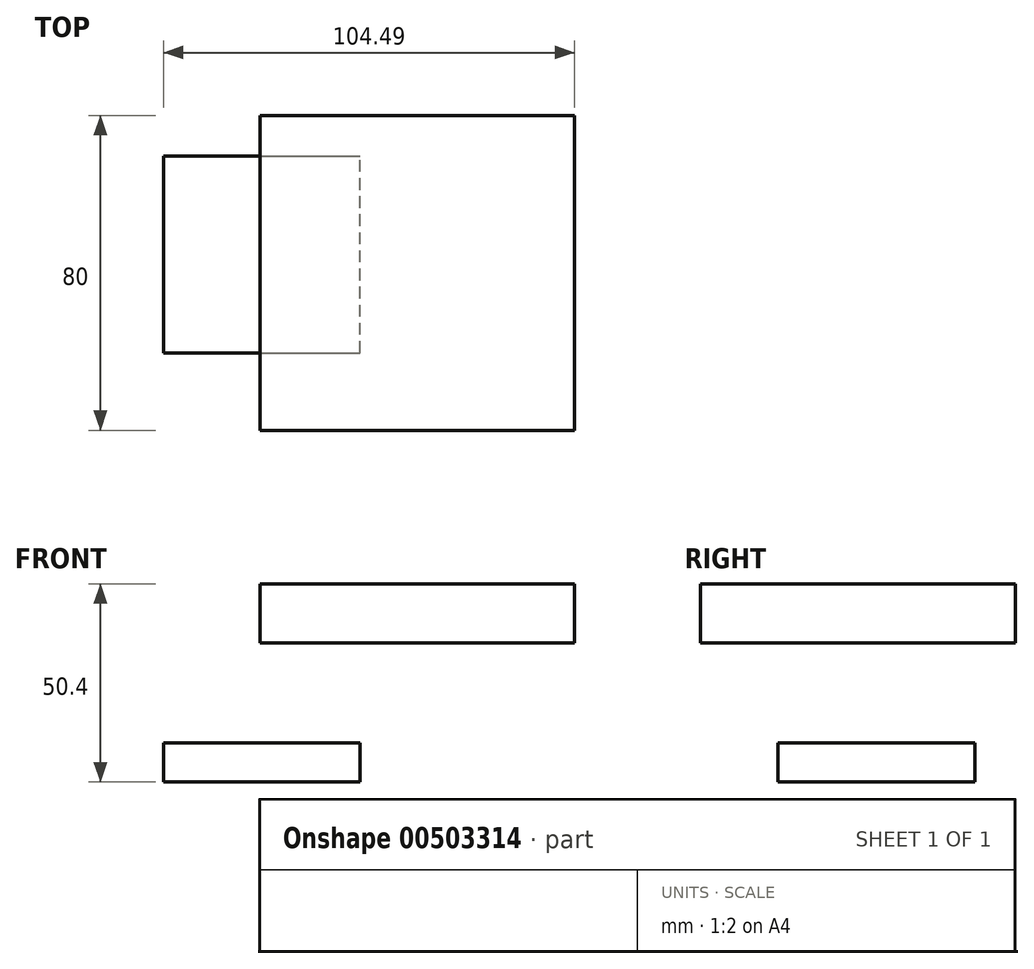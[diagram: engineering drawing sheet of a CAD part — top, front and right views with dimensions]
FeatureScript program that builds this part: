
annotation { "Feature Type Name" : "Feature", "Feature Type Description" : "" }
export const myFeature = defineFeature(function(context is Context, id is Id, definition is map)
    precondition{}
    {
        {
            var Q0;
            Q0=qCreatedBy(makeId("Top.planeOp"),FACE);
            var sketch = newSketch(context, id + "F0", { "sketchPlane" : qUnion([Q0])});
            skLineSegment(sketch, "E0.bottom", {"start": v(0, 0) * mm, "end": v(80, 0) * mm});
            skLineSegment(sketch, "E0.top", {"start": v(0, -80) * mm, "end": v(80, -80) * mm});
            skLineSegment(sketch, "E0.left", {"start": v(0, 0) * mm, "end": v(0, -80) * mm});
            skLineSegment(sketch, "E0.right", {"start": v(80, 0) * mm, "end": v(80, -80) * mm});
            skSolve(sketch);
        }
        {
            var Q0;
            Q0=makeQuery(id+"F0.imprint","IMPRINT",FACE,{"disambiguationData":[TD([[makeQuery(id+"F0.imprint","IMPRINT",EDGE,{"derivedFrom":sQuery(id+"F0.wireOp",EDGE,"E0.bottom")}),-1.0]])]});
            extrude(context, id + "F1", {"entities" : qUnion([Q0]), "depth" : 15 * mm, "offsetDistance" : 25.4 * mm});
        }
        {
            var Q0;
            Q0=makeQuery(id+"F1.opExtrude","CAP_FACE",FACE,{"disambiguationData":[OSD([sQuery(id+"F0.wireOp",EDGE,"E0.bottom"),sQuery(id+"F0.wireOp",EDGE,"E0.top"),sQuery(id+"F0.wireOp",EDGE,"E0.left"),sQuery(id+"F0.wireOp",EDGE,"E0.right")])],"isStart":true});
            cPlane(context, id + "F2", {"entities" : qUnion([Q0]), "cplaneType" : CPlaneType.OFFSET, "offset" : 25.4 * mm, "width" : 152.4 * mm, "height" : 152.4 * mm});
        }
        {
            var Q0;
            Q0=qCreatedBy(id+"F2.planeOp",FACE);
            var sketch = newSketch(context, id + "F3", { "sketchPlane" : qUnion([Q0])});
            skLineSegment(sketch, "E1.bottom", {"start": v(-24.5, 60.32) * mm, "end": v(25.5, 60.32) * mm});
            skLineSegment(sketch, "E1.top", {"start": v(-24.5, 10.32) * mm, "end": v(25.5, 10.32) * mm});
            skLineSegment(sketch, "E1.left", {"start": v(-24.5, 60.32) * mm, "end": v(-24.5, 10.32) * mm});
            skLineSegment(sketch, "E1.right", {"start": v(25.5, 60.32) * mm, "end": v(25.5, 10.32) * mm});
            skSolve(sketch);
        }
        {
            var Q0;
            Q0=makeQuery(id+"F3.imprint","IMPRINT",FACE,{"disambiguationData":[TD([[makeQuery(id+"F3.imprint","IMPRINT",EDGE,{"derivedFrom":sQuery(id+"F3.wireOp",EDGE,"E1.bottom")}),-1.0]])]});
            extrude(context, id + "F4", {"entities" : qUnion([Q0]), "depth" : 10 * mm, "offsetDistance" : 25.4 * mm});
        }
    });
